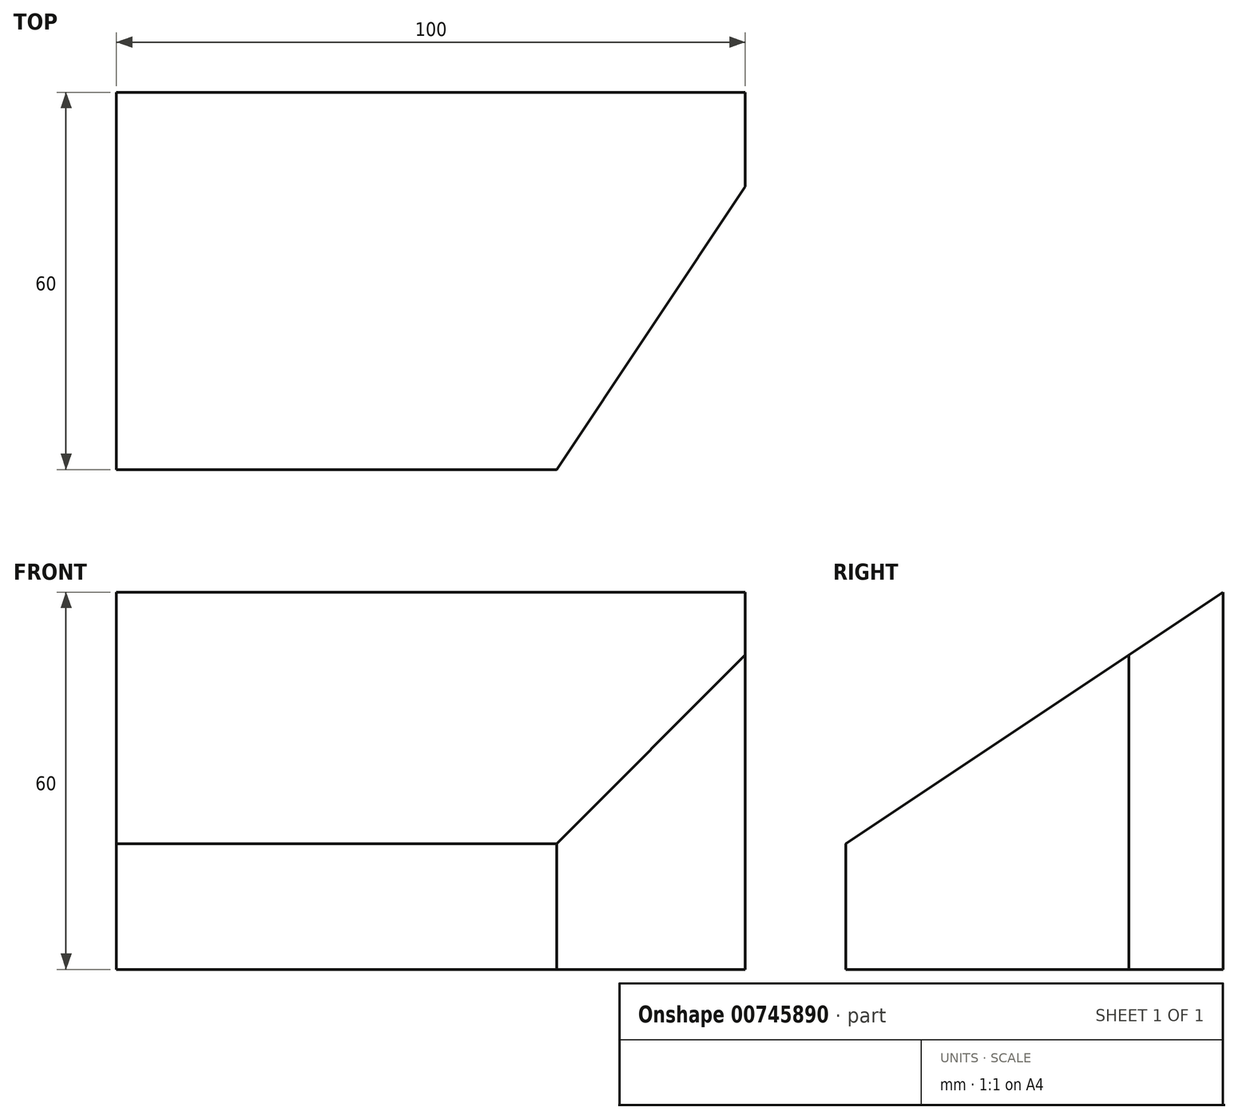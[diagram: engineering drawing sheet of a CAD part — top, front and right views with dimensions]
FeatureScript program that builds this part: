
annotation { "Feature Type Name" : "Feature", "Feature Type Description" : "" }
export const myFeature = defineFeature(function(context is Context, id is Id, definition is map)
    precondition{}
    {
        {
            var Q0;
            Q0=qCreatedBy(makeId("Front.planeOp"),FACE);
            var sketch = newSketch(context, id + "F0", { "sketchPlane" : qUnion([Q0])});
            skLineSegment(sketch, "E0.bottom", {"start": v(0, 0) * mm, "end": v(100, 0) * mm});
            skLineSegment(sketch, "E0.top", {"start": v(0, 60) * mm, "end": v(100, 60) * mm});
            skLineSegment(sketch, "E0.left", {"start": v(0, 0) * mm, "end": v(0, 60) * mm});
            skLineSegment(sketch, "E0.right", {"start": v(100, 0) * mm, "end": v(100, 60) * mm});
            skLineSegment(sketch, "E1.bottom", {"start": v(0, 0) * mm, "end": v(70, 0) * mm});
            skLineSegment(sketch, "E1.top", {"start": v(0, 20) * mm, "end": v(70, 20) * mm});
            skLineSegment(sketch, "E1.left", {"start": v(0, 0) * mm, "end": v(0, 20) * mm});
            skLineSegment(sketch, "E1.right", {"start": v(70, 0) * mm, "end": v(70, 20) * mm});
            skLineSegment(sketch, "E2", {"start": v(70, 20) * mm, "end": v(100, 20) * mm, "construction": true});
            skLineSegment(sketch, "E3", {"start": v(70, 20) * mm, "end": v(70, 60) * mm, "construction": true});
            skSolve(sketch);
        }
        {
            var Q0;
            Q0 = qSketchRegion(id + "F0", true);
            extrude(context, id + "F1", {"entities" : qUnion([Q0]), "oppositeDirection" : true, "depth" : 60 * mm, "offsetDistance" : 25 * mm});
        }
        {
            var Q0;
            Q0=makeQuery(id+"F1.opExtrude","SWEPT_FACE",FACE,{"disambiguationData":[OSD([sQuery(id+"F0.wireOp",EDGE,"E0.right")])]});
            var sketch = newSketch(context, id + "F2", { "sketchPlane" : qUnion([Q0])});
            skLineSegment(sketch, "E4", {"start": v(0, 20) * mm, "end": v(0, 0) * mm});
            skLineSegment(sketch, "E5", {"start": v(0, 0) * mm, "end": v(60, 0) * mm});
            skLineSegment(sketch, "E6", {"start": v(60, 0) * mm, "end": v(60, 60) * mm});
            skLineSegment(sketch, "E7", {"start": v(60, 60) * mm, "end": v(0, 20) * mm});
            skLineSegment(sketch, "E8", {"start": v(45, 50) * mm, "end": v(45, 0) * mm});
            skSolve(sketch);
        }
        {
            var Q0;
            Q0=makeQuery(id+"F1.opExtrude","SWEPT_FACE",FACE,{"disambiguationData":[OSD([sQuery(id+"F0.wireOp",EDGE,"E0.top")])]});
            var sketch = newSketch(context, id + "F3", { "sketchPlane" : qUnion([Q0])});
            skLineSegment(sketch, "E9", {"start": v(70, 0) * mm, "end": v(100, 45) * mm});
            skLineSegment(sketch, "E10", {"start": v(100, 45) * mm, "end": v(100, 60) * mm});
            skLineSegment(sketch, "E11", {"start": v(100, 60) * mm, "end": v(0, 60) * mm});
            skLineSegment(sketch, "E12", {"start": v(0, 60) * mm, "end": v(0, 0) * mm});
            skLineSegment(sketch, "E13", {"start": v(0, 0) * mm, "end": v(70, 0) * mm});
            skSolve(sketch);
        }
        {
            var Q0;
            {var subQ0=sQuery(id+"F3.wireOp",EDGE,"E9");Q0=makeQuery(id+"F3.imprint","IMPRINT",FACE,{"disambiguationData":[TD([[makeQuery(id+"F3.imprint","IMPRINT",EDGE,{"derivedFrom":subQ0}),-1.0]])]});}
            extrude(context, id + "F4", {"entities" : qUnion([Q0]), "operationType" : NewBodyOperationType.REMOVE, "endBound" : BoundingType.THROUGH_ALL, "oppositeDirection" : true, "depth" : 25 * mm, "offsetDistance" : 25 * mm});
        }
        {
            var Q0;
            {var subQ1=sQuery(id+"F0.wireOp",EDGE,"E0.right");var subQ2=makeQuery(id+"F1.opExtrude","SWEPT_EDGE",EDGE,{"disambiguationData":[OSD([sQuery(id+"F0.wireOp",EDGE,"E0.top"),subQ1])]});Q0=makeQuery(id+"F2.imprint","IMPRINT",FACE,{"disambiguationData":[TD([[makeQuery(id+"F2.imprint","IMPRINT",EDGE,{"derivedFrom":subQ2}),1.0]])]});}
            extrude(context, id + "F5", {"entities" : qUnion([Q0]), "operationType" : NewBodyOperationType.REMOVE, "endBound" : BoundingType.THROUGH_ALL, "oppositeDirection" : true, "depth" : 25 * mm, "offsetDistance" : 25 * mm});
        }
    });
